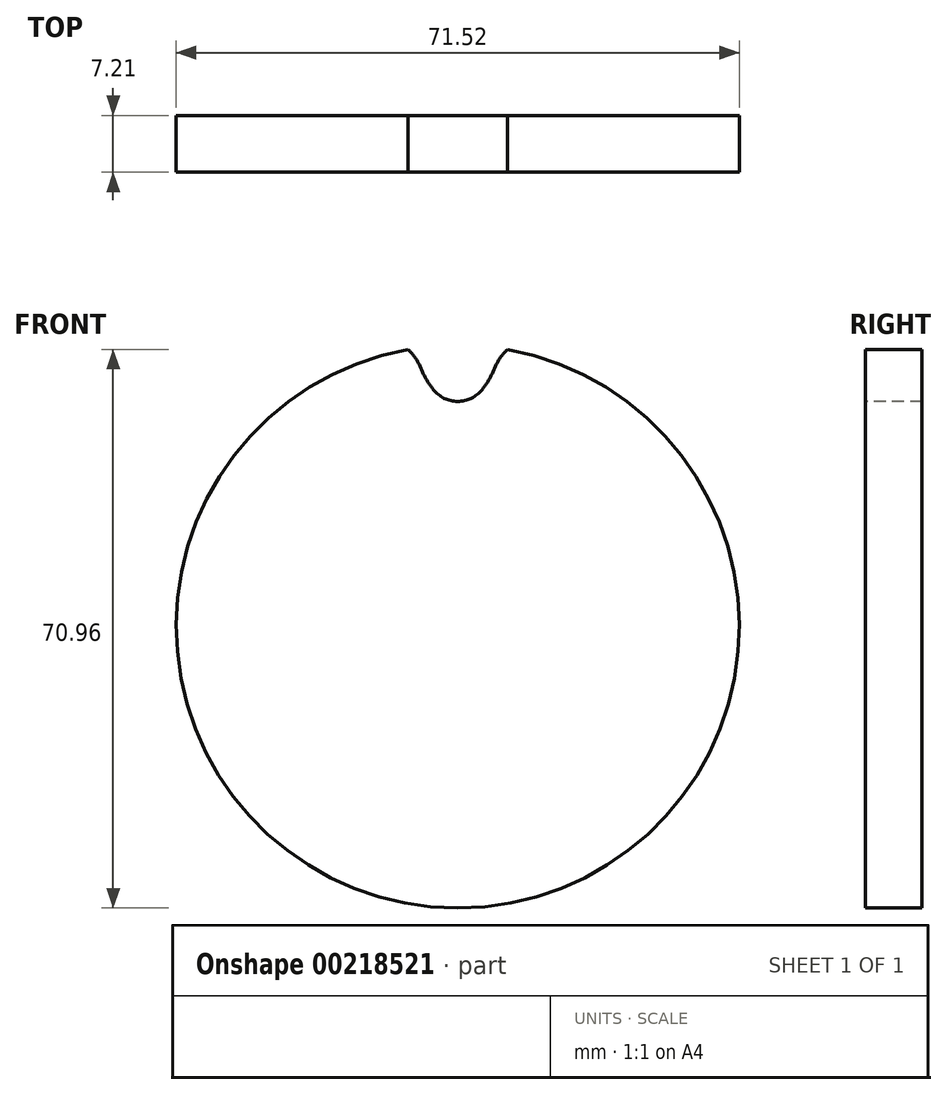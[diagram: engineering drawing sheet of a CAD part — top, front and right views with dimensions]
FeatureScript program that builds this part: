
annotation { "Feature Type Name" : "Feature", "Feature Type Description" : "" }
export const myFeature = defineFeature(function(context is Context, id is Id, definition is map)
    precondition{}
    {
        {
            var Q0;
            Q0=qCreatedBy(makeId("Front.planeOp"),FACE);
            var sketch = newSketch(context, id + "F0", { "sketchPlane" : qUnion([Q0])});
            skCircle(sketch, "E0", {"center": v(0, 0) * mm, "radius": 35.76 * mm});
            skSolve(sketch);
        }
        {
            var Q0;
            Q0 = qSketchRegion(id + "F0", true);
            extrude(context, id + "F1", {"entities" : qUnion([Q0]), "oppositeDirection" : true, "depth" : 7.2 * mm});
        }
        {
            var Q0;
            Q0=makeQuery(id+"F1.opExtrude","CAP_FACE",FACE,{"disambiguationData":[OSD([sQuery(id+"F0.wireOp",EDGE,"E0")])],"isStart":true});
            var sketch = newSketch(context, id + "F2", { "sketchPlane" : qUnion([Q0])});
            skCircle(sketch, "E1", {"center": v(0, 0) * mm, "radius": 32.55 * mm, "construction": true});
            skLineSegment(sketch, "E2", {"start": v(0, 0) * mm, "end": v(0, 32.55) * mm, "construction": true});
            skLineSegment(sketch, "E3", {"start": v(0, 32.55) * mm, "end": v(75.89, 32.55) * mm, "construction": true});
            skLineSegment(sketch, "E4", {"start": v(0, 32.55) * mm, "end": v(5, 36.56) * mm, "construction": true});
            skLineSegment(sketch, "E5", {"start": v(5, 36.56) * mm, "end": v(-4.46, 32.3) * mm, "construction": true});
            skLineSegment(sketch, "E6", {"start": v(-4.46, 32.3) * mm, "end": v(-4.82, 33.1) * mm});
            skLineSegment(sketch, "E7", {"start": v(0, 0) * mm, "end": v(-7.13, 35.85) * mm, "construction": true});
            skArc(sketch, "E8", {"start": v(-7.13, 35.85) * mm, "mid": v(-15.87, 26.15) * mm, "end": v(-4.82, 33.1) * mm, "construction": true});
            skArc(sketch, "E9", {"start": v(-4.82, 33.1) * mm, "mid": v(-5.78, 34.63) * mm, "end": v(-7.13, 35.85) * mm});
            skLineSegment(sketch, "E10", {"start": v(0.64, 20.98) * mm, "end": v(-4.82, 33.1) * mm, "construction": true});
            skArc(sketch, "E11", {"start": v(-4.46, 32.3) * mm, "mid": v(-3.84, 31.14) * mm, "end": v(-3.1, 30.07) * mm});
            skArc(sketch, "E12", {"start": v(-3.1, 30.07) * mm, "mid": v(13.83, 41.97) * mm, "end": v(-4.46, 32.3) * mm, "construction": true});
            skArc(sketch, "E13.0.MirrorCS", {"start": v(4.46, 32.3) * mm, "mid": v(3.84, 31.14) * mm, "end": v(3.1, 30.07) * mm});
            skLineSegment(sketch, "E14.0.MirrorCS", {"start": v(4.46, 32.3) * mm, "end": v(4.82, 33.1) * mm});
            skArc(sketch, "E15.0.MirrorCS", {"start": v(4.82, 33.1) * mm, "mid": v(5.78, 34.63) * mm, "end": v(7.13, 35.85) * mm});
            skArc(sketch, "E16", {"start": v(-3.1, 30.07) * mm, "mid": v(0, 28.59) * mm, "end": v(3.1, 30.07) * mm});
            skArc(sketch, "E17", {"start": v(3.1, 30.07) * mm, "mid": v(0, 36.51) * mm, "end": v(-3.1, 30.07) * mm, "construction": true});
            skLineSegment(sketch, "E18.anchor1", {"start": v(0, 0) * mm, "end": v(4.82, 33.1) * mm, "construction": true});
            skLineSegment(sketch, "E18.anchor2", {"start": v(0, 0) * mm, "end": v(4.82, 33.1) * mm, "construction": true});
            skArc(sketch, "E19", {"start": v(7.13, 35.85) * mm, "mid": v(0, 37.75) * mm, "end": v(-7.13, 35.85) * mm});
            skSolve(sketch);
        }
        {
            var Q0;
            {var subQ4=sQuery(id+"F2.wireOp",EDGE,"E6");Q0=makeQuery(id+"F2.imprint","IMPRINT",FACE,{"disambiguationData":[TD([[makeQuery(id+"F2.imprint","IMPRINT",EDGE,{"derivedFrom":subQ4}),-1.0]])]});}
            extrude(context, id + "F3", {"entities" : qUnion([Q0]), "operationType" : NewBodyOperationType.REMOVE, "endBound" : BoundingType.THROUGH_ALL, "oppositeDirection" : true, "depth" : 25.4 * mm});
        }
    });
